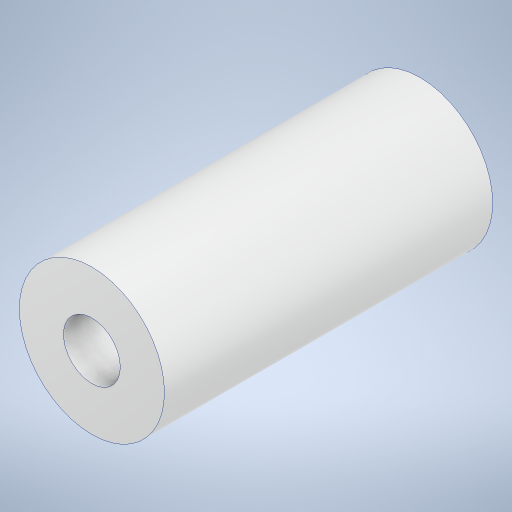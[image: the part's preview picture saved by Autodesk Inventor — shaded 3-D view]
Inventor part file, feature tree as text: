
AUTODESK INVENTOR PART (.ipt)
format: ipt  version: 2024 (Build 280153000, 153)  size: 219,136 bytes
history: native  units: in
note: dims shown in document units (in); Inventor stores cm internally (conversion verified against a paired STEP export)
features: extrude x1, sketch x1
ambient origin geometry x8: Origin, YZ Plane, XZ Plane, XY Plane, X Axis, Y Axis, Z Axis, Center Point
bodies: Solid1 (feature_tree)
feature tree (2):
  extrude  "Extrusion1"  Depth=1.131in
  sketch  "Sketch1"  dims[d0=0.196in d1=0.5in d2=1.131in d3=0.0in]
